# Revit family: Equipment-Gym-Draper_Inc.-Forward_Folding_Backstop-TF-20
name_source: partatom
category: Specialty Equipment
units: mm (PartAtom-declared; Revit-internal decimal feet)

## family parameters
Always vertical = Yes
Classification Number = 23.40.50.34.14.11
Cut with Voids When Loaded = No
Enable Cutting in Views = No
Maintain Annotation Orientation = No
Part Type = Normal
Room Calculation Point = No
Round Connector Dimension = Use Diameter
Shared = No
Work Plane-Based = No

## types (11) — shared parameters
Apparent Load = 746 VA
Backboard Frame = Metal - Draper Inc. - Aluminum
Backboard Length = 6' - 0"
Default Elevation = 0"
Description = Basketball Backstop
Frame = Metal - Draper Inc. - White Paint
Frequency = 60 Hz
Manufacturer = Draper Inc.
Model = TF-20
Number of Poles = 1
Power Factor = 1
Product Documentation Link = http://www.draperinc.com
Product Name = Forward Folding Basketball Backstops
Product Page URL = http://www.draperinc.com
URL = http://www.draperinc.com
Voltage = 120 V

## per-type parameters (varying)
| type | Backboard | Backboard Height | C | Constraint C | Fan Backstop | Rect Backstop | Stripe |
| 503143 Fan Aluminum | Metal - Draper Inc. - Aluminum - White Paint | 3' - 6" | 10 3/16" | 10 3/16" | Yes | No | Paintl - Draper Inc. - Red Paint |
| 503148 Fan Fiberglass | Plastic - Draper Inc. - Fiberglass - White | 3' - 6" | 10 1/2" | 10 1/2" | Yes | No | Paintl - Draper Inc. - Red Paint |
| 5031500 Fan Glass | Glass - Draper Inc. - Backboard Glass | 3' - 6" | 11" | 11" | Yes | No | Metal - Draper Inc. - White Paint |
| 503167 72" x 42" Rectangular Steel | Metal - Draper Inc. - Steel - White Paint | 3' - 6" | 10 1/2" | 10 1/2" | No | Yes | Paintl - Draper Inc. - Red Paint |
| 503154 72" x 48" Rectangular Steel | Metal - Draper Inc. - Steel - White Paint | 4' - 0" | 10 1/2" | 10 1/2" | No | Yes | Paintl - Draper Inc. - Red Paint |
| 503144 72" x 42" Rect. Fiberglass | Plastic - Draper Inc. - Fiberglass - White | 3' - 6" | 10 1/2" | 10 1/2" | No | Yes | Paintl - Draper Inc. - Red Paint |
| 503153 72" x 48" Rect. Fiberglass | Plastic - Draper Inc. - Fiberglass - White | 4' - 0" | 10 1/2" | 10 1/2" | No | Yes | Paintl - Draper Inc. - Red Paint |
| 503140 72" x 42" Rect. Wood | Wood - Draper Inc. - White Paint | 3' - 6" | 10 9/16" | 10 9/16" | No | Yes | Paintl - Draper Inc. - Red Paint |
| 503151 72" x 48" Rect. Wood | Wood - Draper Inc. - White Paint | 4' - 0" | 11 1/8" | 11 1/8" | No | Yes | Paintl - Draper Inc. - Red Paint |
| 503136 72" x 42" Rect. Glass | Glass - Draper Inc. - Backboard Glass | 3' - 6" | 11 1/4" | 11 1/4" | No | Yes | Metal - Draper Inc. - White Paint |
| 503152 72" x 48" Rect. Glass | Glass - Draper Inc. - Backboard Glass | 4' - 0" | 11 1/4" | 11 1/4" | No | Yes | Metal - Draper Inc. - White Paint |

## geometry (parser evidence)
native form markers: Blend x2, Sweep x11
no freeform markers — native parametric forms only
